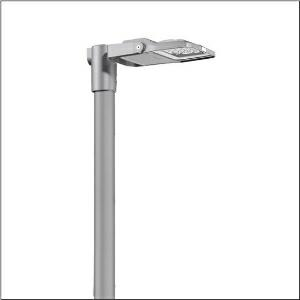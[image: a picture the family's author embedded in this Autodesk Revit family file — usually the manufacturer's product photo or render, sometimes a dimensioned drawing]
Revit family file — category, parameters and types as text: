
# Revit family: floodlight_fl_21_iq_micro___pl43_5xa7761a4a3a_9f97
name_source: partatom
category: Lighting Fixtures
units: mm (PartAtom-declared; Revit-internal decimal feet)

## family parameters
Cut with Voids When Loaded = No
Host = Face
Light Source = No
Part Type = Normal
Room Calculation Point = No
Round Connector Dimension = Use Diameter
Shared = No

## types (1)
- --- (1 x LED, 3170 lm, 23.1 W, 4000K)
    Apparent Load = 23 VA
    CIE Flux Codes = 29 80 99 100 100
    Color Rendering = 70
    Color Temperature = 4000K
    Default Elevation = 1800 mm
    Description = Floodlight FL 21 iQ micro, floodlight, primary light control with lens, of PMMA, primary optical cover: protective disc, of toughened safety glass, transparent, light distribution: PL43, light emission: direct distribution, installation type: surface-mounted, LED, High Power LED, rated luminous flux: 3.170lm, luminous efficacy: 137lm/W, light colour: 740, colour temperature: 4000K, control gear: iQ Comfort/DALI, control: optimised constant luminous flux control (CLO 2.0), Desk-Remote (wireless, voltage-free reading and setting of iQ features in the workshop via application-optimized NFC function/RFID function), Light-Fading, Smart-Wire, Night-Set, Lumen-Switch, Temp-Guard, Auto-Match, with terminal, 6-pole, mains connection: 220..240V, AC, 50/60Hz, start of lifetime: 23W, end of service life: 24W, reduction: 11W, luminaire housing, of diecast aluminium, powder-coated, Siteco® metallic grey (DB 702S), corrosivity category C5 mid according to DIN EN ISO 12944, suitable for swimming pools, chlorine-resistant, sealing non-destructively replaceable, please order mast flange separately, mast bracket, of steel, galvanised, powder-coated, Siteco® metallic grey (DB 702S), protection rating (complete): IP66, insulation class (complete): insulation class II (safety insulation), certification: CE, ENEC, VDE, protection symbol: D, impact resistance: IK07, permissible operating ambient temperature: -40..+40°C, permissible operating ambient temperature for outdoor applications: -40..+50°C, standard: DIN EN 12944, LABS conformity tested according to VDMA 24364:2018-05, packaging unit: 1 piece

Light Distribution: PL43
    Height = 65 mm
    Lamp = 1 x LED
    Lamp Light Flux = 3170 lm
    Lamp Power = 23.1 W
    Lamp count = 1
    Length = 312 mm
    Luminous efficacy = 137 lm/W
    Manufacturer = Siteco
    ModVariant = No
    Model = 5XA7761A4A3A
    Number of Poles = 1
    OnlyDefault = Yes
    Power Factor = 1
    Product Name = Floodlight FL 21 iQ micro | PL43
    Product group = floodlight | pylon annexe
    ProductGroupID = 6200
    Protection Class = Protection class II
    Protection Degree = IP 66
    RLX_Detail_Level = 1
    RLX_Emergency_Light_Flux = 0 lm
    RLX_Emergency_Type = 0
    RLX_Emergency_Type_DB = No
    RlxData = <blob elided: 101753 chars, md5=63728129>
    Socket = socket
    Standby Power = 0 W
    System Light Flux = 3170 lm
    System Power = 23 W
    Type Comments = factory setting: luminous flux: 100 % | dim-lin: 254 | 455 mA
    Type Image = l_1007121.jpg
    URL = http://relux.com
    VarID = @adj_176720
    Voltage = 0 V
    Weight = 0.00 kg
    Width = 230 mm

## geometry (parser evidence)
native form markers: Blend x4, Sweep x11
no freeform markers — native parametric forms only
